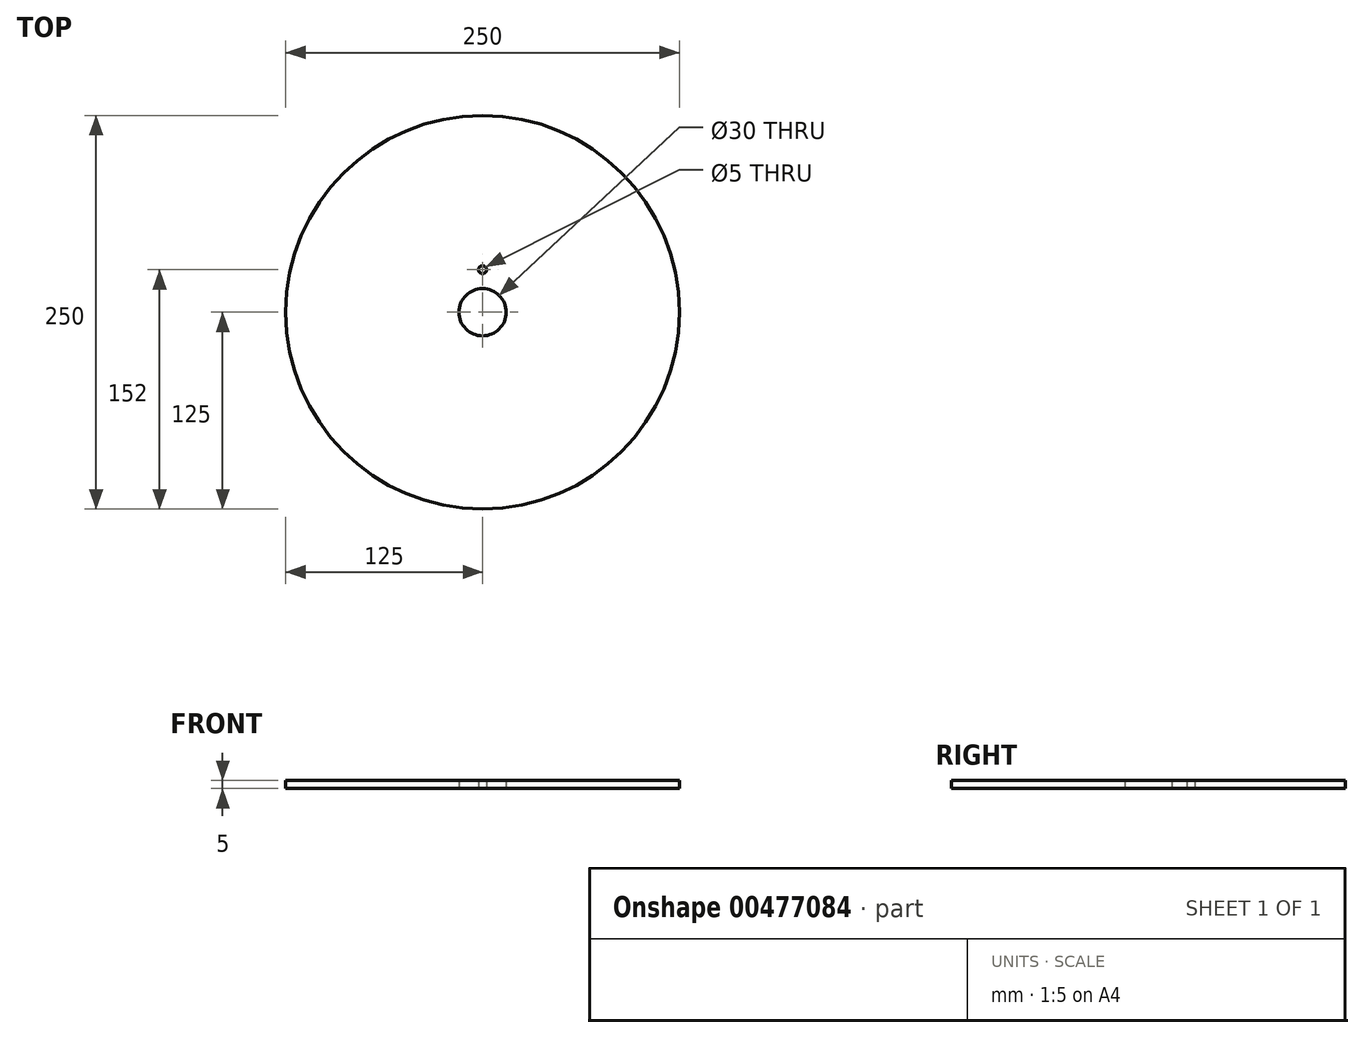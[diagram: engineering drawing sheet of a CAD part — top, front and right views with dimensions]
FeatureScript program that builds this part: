
annotation { "Feature Type Name" : "Feature", "Feature Type Description" : "" }
export const myFeature = defineFeature(function(context is Context, id is Id, definition is map)
    precondition{}
    {
        {
            var Q0;
            Q0=qCreatedBy(makeId("Top.planeOp"),FACE);
            var sketch = newSketch(context, id + "F0", { "sketchPlane" : qUnion([Q0])});
            skCircle(sketch, "E0", {"center": v(0, 0) * mm, "radius": 125 * mm});
            skSolve(sketch);
        }
        {
            var Q0;
            Q0=qCreatedBy(makeId("Top.planeOp"),FACE);
            var sketch = newSketch(context, id + "F1", { "sketchPlane" : qUnion([Q0])});
            skCircle(sketch, "E1", {"center": v(0, 0) * mm, "radius": 15 * mm});
            skSolve(sketch);
        }
        {
            var Q0;
            Q0 = qSketchRegion(id + "F0", true);
            extrude(context, id + "F2", {"entities" : qUnion([Q0]), "depth" : 5 * mm});
        }
        {
            var Q0;
            Q0 = qSketchRegion(id + "F1", true);
            extrude(context, id + "F3", {"entities" : qUnion([Q0]), "operationType" : NewBodyOperationType.REMOVE, "endBound" : BoundingType.THROUGH_ALL, "depth" : 25 * mm});
        }
        {
            var Q0;
            Q0=qCreatedBy(makeId("Top.planeOp"),FACE);
            var sketch = newSketch(context, id + "F4", { "sketchPlane" : qUnion([Q0])});
            skPoint(sketch, "E2", {"position": v(0, 27) * mm});
            skSolve(sketch);
        }
        {
            var Q0;
            Q0=sQuery(id+"FG1mpqwHBa5KMn2_1.1.F4.wireOp",VERTEX,"E2");
            var Q1;
            Q1=sQuery(id+"FG1mpqwHBa5KMn2_1.2.F4.wireOp",VERTEX,"E2");
            var Q2;
            Q2=sQuery(id+"FG1mpqwHBa5KMn2_1.3.F4.wireOp",VERTEX,"E2");
            var Q3;
            Q3=sQuery(id+"F4.wireOp",VERTEX,"E2");
            var Q4;
            Q4=makeQuery(id+"F2.opExtrude","SWEPT_BODY",BODY,{"disambiguationData":[OSD([sQuery(id+"F0.wireOp",EDGE,"E0")])]});
            hole(context, id + "F5", {"style" : HoleStyle.SIMPLE, "endStyle" : HoleEndStyle.THROUGH, "oppositeDirection" : true, "standardTappedOrClearance" : lookupTablePath({ "standard" : "ISO", "size" : "5", "type" : "Drilled" }), "standardBlindInLast" : lookupTablePath({ "standard" : "ISO", "size" : "5", "type" : "Drilled" }), "holeDiameter" : 5 * mm, "isTappedThrough" : true, "tappedDepth" : 12 * mm, "tapClearance" : 3, "locations" : qUnion([Q0, Q1, Q2, Q3]), "scope" : qUnion([Q4])});
        }
    });
